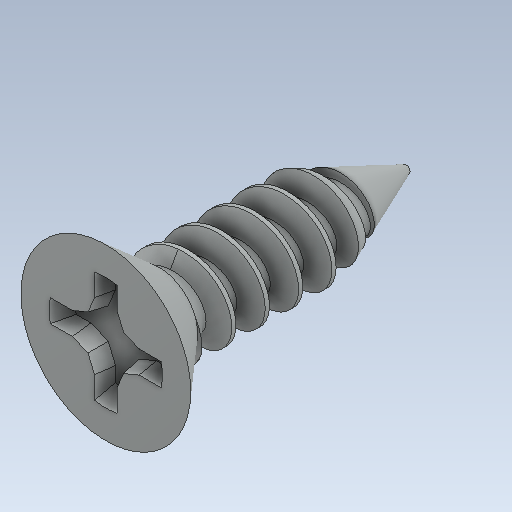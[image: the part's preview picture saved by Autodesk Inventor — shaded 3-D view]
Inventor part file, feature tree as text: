
AUTODESK INVENTOR PART (.ipt)
format: ipt  version: 2020 (Build 240168000, 168)  size: 418,816 bytes
history: native  units: mm
features: revolve x1
ambient origin geometry x8: Origin, YZ Plane, XZ Plane, XY Plane, X Axis, Y Axis, Z Axis, Center Point
bodies: Solid1 (feature_tree)
feature tree (1):
  revolve  "Revolve2"  [1 undecoded]
note: 1 required parameter value undecoded (feature->parameter linkage not recoverable at this tier; creation-order binding heuristic only, values carry confidence <= 0.55)
